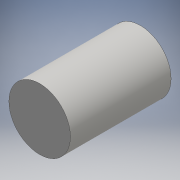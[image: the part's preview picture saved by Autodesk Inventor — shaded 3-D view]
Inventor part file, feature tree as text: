
AUTODESK INVENTOR PART (.ipt)
format: ipt  version: 2016 (Build 200138000, 138)  size: 86,016 bytes
history: native  units: mm
features: other x1, extrude x1, sketch x1
ambient origin geometry x8: Origin, YZ Plane, XZ Plane, XY Plane, X Axis, Y Axis, Z Axis, Center Point
bodies: Body1 (feature_tree)
feature tree (3):
  other  "ソリッド1"
  extrude  "押し出し1"  Depth=44.0mm
  sketch  "スケッチ1"
